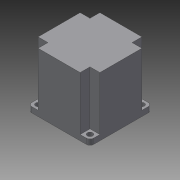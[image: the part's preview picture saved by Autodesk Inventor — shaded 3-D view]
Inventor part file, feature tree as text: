
AUTODESK INVENTOR PART (.ipt)
format: ipt  version: 2015 (Build 190159000, 159)  size: 141,824 bytes
history: native  units: in
note: dims shown in document units (in); Inventor stores cm internally (conversion verified against a paired STEP export)
features: extrude x4, sketch x3, fillet x1
ambient origin geometry x8: Origin, YZ Plane, XZ Plane, XY Plane, X Axis, Y Axis, Z Axis, Center Point
bodies: Solid1 (feature_tree)
feature tree (8):
  sketch  "Sketch1"  dims[d0=2.2205in d1=2.2205in]
  extrude  "Extrusion1"  Depth=2.2205in
  extrude  "Extrusion2"  Depth=0.3543in
  fillet  "Fillet1"  Radius=2.126in
  extrude  "Extrusion3"  Depth=0.8268in
  extrude  "Extrusion4"  Depth=0.1969in
  sketch  "Sketch2"  dims[d2=0.3543in d3=0.3543in d4=2.126in d5=0.0in]
  sketch  "Sketch3"  dims[d6=1.8559in d7=1.8559in d8=0.1969in d9=0.1969in d10=0.0in d11=0.125in d12=1.5in d13=0.063in d14=0.0in d15=0.25in d16=0.8268in d17=0.0in]
